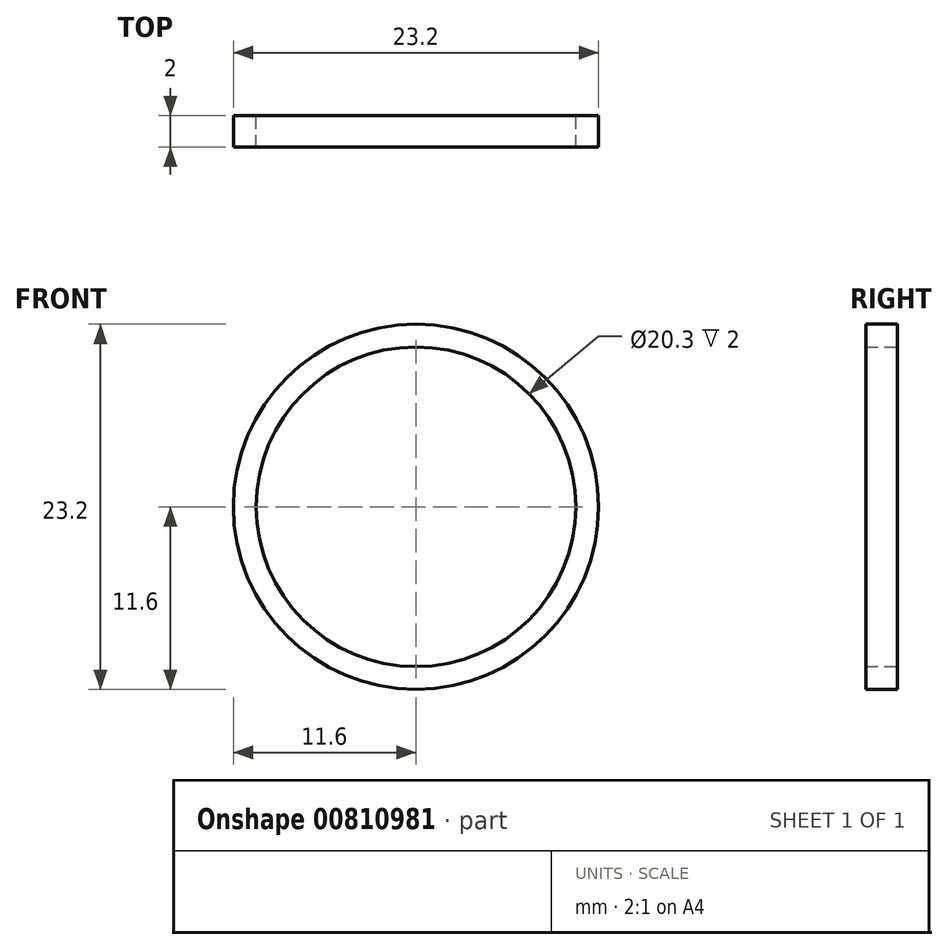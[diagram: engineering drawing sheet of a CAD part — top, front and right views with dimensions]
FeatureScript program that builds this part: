
annotation { "Feature Type Name" : "Feature", "Feature Type Description" : "" }
export const myFeature = defineFeature(function(context is Context, id is Id, definition is map)
    precondition{}
    {
        {
            var Q0;
            Q0=qCreatedBy(makeId("Front.planeOp"),FACE);
            var sketch = newSketch(context, id + "F0", { "sketchPlane" : qUnion([Q0])});
            skCircle(sketch, "E0", {"center": v(0, 0) * mm, "radius": 10.15 * mm});
            skCircle(sketch, "E1", {"center": v(0, 0) * mm, "radius": 11.6 * mm});
            skSolve(sketch);
        }
        {
            var Q0;
            Q0=makeQuery(id+"F0.imprint","IMPRINT",FACE,{"disambiguationData":[TD([[makeQuery(id+"F0.imprint","IMPRINT",EDGE,{"derivedFrom":sQuery(id+"F0.wireOp",EDGE,"E0")}),-1.0]])]});
            extrude(context, id + "F1", {"entities" : qUnion([Q0]), "depth" : 2 * mm, "offsetDistance" : 25 * mm});
        }
    });
